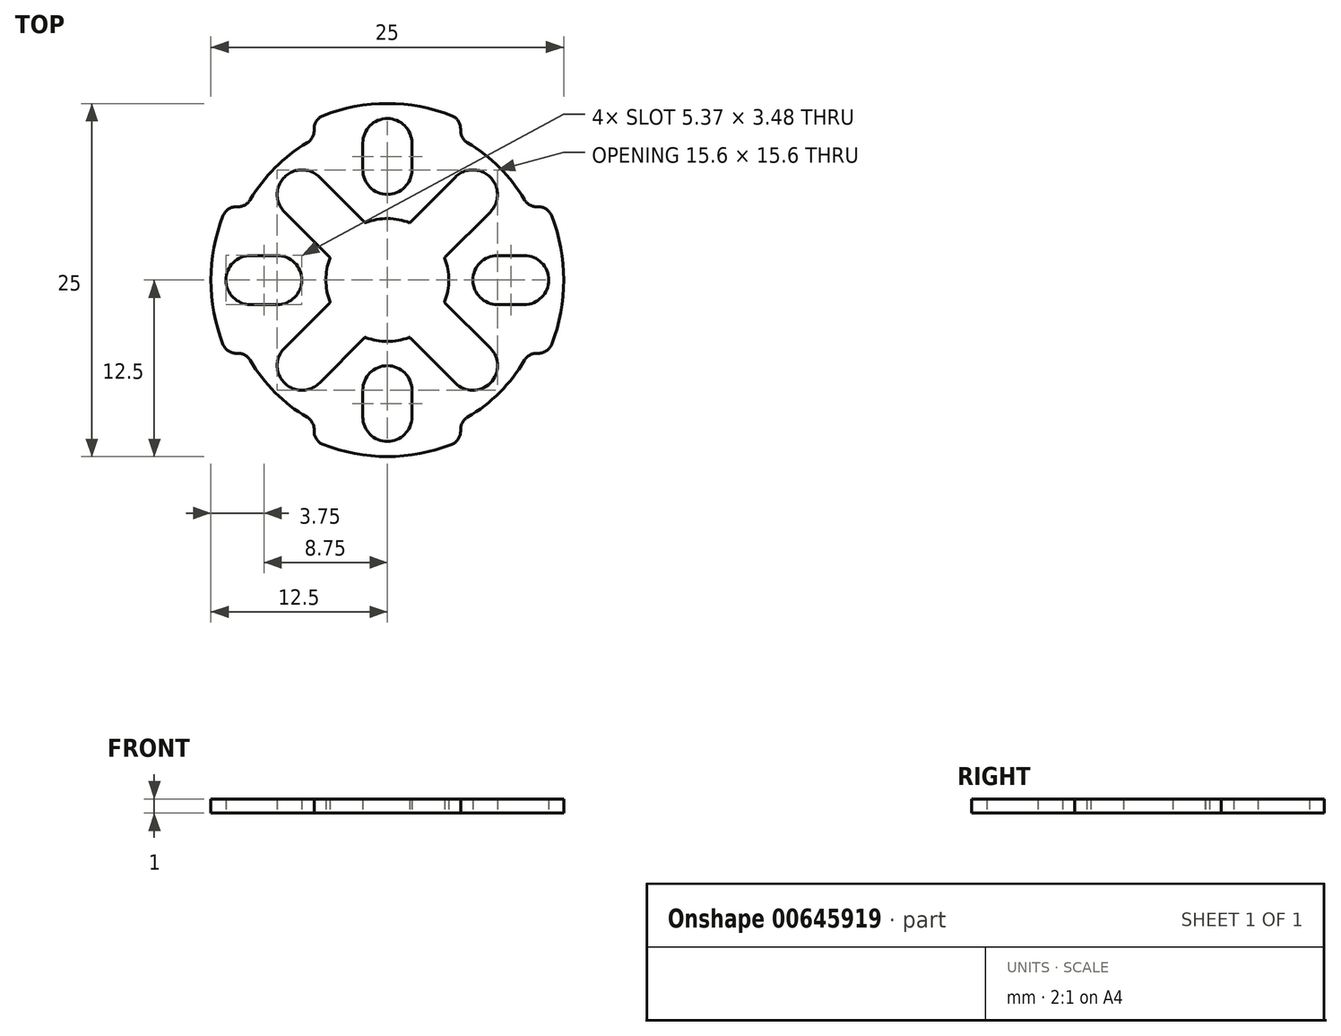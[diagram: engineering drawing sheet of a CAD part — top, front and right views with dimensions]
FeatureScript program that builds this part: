
annotation { "Feature Type Name" : "Feature", "Feature Type Description" : "" }
export const myFeature = defineFeature(function(context is Context, id is Id, definition is map)
    precondition{}
    {
        {
            var Q0;
            Q0=qCreatedBy(makeId("Top.planeOp"),FACE);
            var sketch = newSketch(context, id + "F0", { "sketchPlane" : qUnion([Q0])});
            skPoint(sketch, "E0.MirrorCS.start.orphan", {"position": v(0, 0) * mm});
            skPoint(sketch, "E1.visualSharp", {"position": v(12.16, 4.72) * mm});
            skPoint(sketch, "E2.MirrorCS.start.orphan", {"position": v(-6.94, 4.47) * mm});
            skPoint(sketch, "E3.orphan", {"position": v(-4.46, 2.26) * mm});
            skPoint(sketch, "E4.center.orphan", {"position": v(-6.07, 6.07) * mm});
            skPoint(sketch, "E5.MirrorCS.end.orphan", {"position": v(4.47, -6.94) * mm});
            skPoint(sketch, "E5.MirrorCS.start.orphan", {"position": v(6.94, -4.47) * mm});
            skPoint(sketch, "E6.start.orphan", {"position": v(-4.47, 6.94) * mm});
            skLineSegment(sketch, "E7", {"start": v(-4.6, 2.13) * mm, "end": v(-7.29, 4.81) * mm});
            skLineSegment(sketch, "E8.MirrorCS", {"start": v(-2.13, 4.6) * mm, "end": v(-4.81, 7.29) * mm});
            skPoint(sketch, "E9.MirrorCS.start.orphan", {"position": v(-4.47, -6.94) * mm});
            skPoint(sketch, "E10.MirrorCS.start.orphan", {"position": v(-6.94, -4.47) * mm});
            skPoint(sketch, "E11.MirrorCS.start.orphan", {"position": v(4.55, -2.08) * mm});
            skPoint(sketch, "E12.MirrorC.end.orphan", {"position": v(4.97, -7.45) * mm});
            skPoint(sketch, "E12.MirrorC.start.orphan", {"position": v(7.45, -4.97) * mm});
            skPoint(sketch, "E13.orphan", {"position": v(-7.45, 4.97) * mm});
            skPoint(sketch, "E14.orphan", {"position": v(-4.97, 7.45) * mm});
            skPoint(sketch, "E15.MirrorCS.end.orphan", {"position": v(4.97, 7.45) * mm});
            skPoint(sketch, "E15.MirrorCS.start.orphan", {"position": v(2.08, 4.55) * mm});
            skPoint(sketch, "E16.MirrorCS.start.orphan", {"position": v(4.55, 2.08) * mm});
            skPoint(sketch, "E17.MirrorCS.end.orphan", {"position": v(-4.97, -7.45) * mm});
            skPoint(sketch, "E17.MirrorCS.start.orphan", {"position": v(-2.08, -4.55) * mm});
            skPoint(sketch, "E18.MirrorCS.start.orphan", {"position": v(-7.45, -4.97) * mm});
            skPoint(sketch, "E19.MirrorCS.start.orphan", {"position": v(-4.55, -2.08) * mm});
            skLineSegment(sketch, "E20.MirrorCS", {"start": v(2.13, 4.6) * mm, "end": v(4.85, 7.32) * mm});
            skArc(sketch, "E21.MirrorCS", {"start": v(4.82, -7.3) * mm, "mid": v(6.06, -7.82) * mm, "end": v(7.3, -7.3) * mm});
            skLineSegment(sketch, "E22.MirrorCS", {"start": v(4.6, -2.13) * mm, "end": v(7.32, -4.85) * mm});
            skLineSegment(sketch, "E23.MirrorCS", {"start": v(-2.13, -4.6) * mm, "end": v(-4.85, -7.32) * mm});
            skLineSegment(sketch, "E24.MirrorCS", {"start": v(-4.6, -2.13) * mm, "end": v(-7.32, -4.85) * mm});
            skLineSegment(sketch, "E25.MirrorCS", {"start": v(2.13, -4.6) * mm, "end": v(4.82, -7.3) * mm});
            skArc(sketch, "E26", {"start": v(4.55, 11.64) * mm, "mid": v(0, 12.5) * mm, "end": v(-4.55, 11.64) * mm});
            skPoint(sketch, "E27.MirrorCS.end.orphan", {"position": v(10.93, 4.72) * mm});
            skPoint(sketch, "E1.filletArc.end.orphan", {"position": v(11.3, 4.72) * mm});
            skArc(sketch, "E28.filletArc", {"start": v(5.19, 10.7) * mm, "mid": v(5.02, 11.27) * mm, "end": v(4.55, 11.64) * mm});
            skArc(sketch, "E29.filletArc", {"start": v(-4.55, 11.64) * mm, "mid": v(-5.02, 11.27) * mm, "end": v(-5.19, 10.7) * mm});
            skArc(sketch, "E30", {"start": v(-5.68, 9.72) * mm, "mid": v(-7.96, 7.96) * mm, "end": v(-9.72, 5.68) * mm});
            skLineSegment(sketch, "E31", {"start": v(-5.19, 10.7) * mm, "end": v(-5.19, 10.58) * mm});
            skLineSegment(sketch, "E32", {"start": v(5.19, 10.7) * mm, "end": v(5.19, 10.58) * mm});
            skPoint(sketch, "E33.visualSharp", {"position": v(-5.19, 9.99) * mm});
            skArc(sketch, "E33.filletArc", {"start": v(-5.68, 9.72) * mm, "mid": v(-5.32, 10.08) * mm, "end": v(-5.19, 10.58) * mm});
            skPoint(sketch, "E34.visualSharp", {"position": v(5.19, 9.99) * mm});
            skArc(sketch, "E34.filletArc", {"start": v(5.19, 10.58) * mm, "mid": v(5.32, 10.08) * mm, "end": v(5.68, 9.72) * mm});
            skArc(sketch, "E35.MirrorCS", {"start": v(-4.55, -11.64) * mm, "mid": v(-5.02, -11.27) * mm, "end": v(-5.19, -10.7) * mm});
            skLineSegment(sketch, "E36.MirrorCS", {"start": v(5.19, -10.7) * mm, "end": v(5.19, -10.58) * mm});
            skArc(sketch, "E37.MirrorCS", {"start": v(5.19, -10.7) * mm, "mid": v(5.02, -11.27) * mm, "end": v(4.55, -11.64) * mm});
            skLineSegment(sketch, "E38.MirrorCS", {"start": v(-5.19, -10.7) * mm, "end": v(-5.19, -10.58) * mm});
            skArc(sketch, "E39.MirrorCS", {"start": v(4.55, -11.64) * mm, "mid": v(0, -12.5) * mm, "end": v(-4.55, -11.64) * mm});
            skPoint(sketch, "E40.MirrorP", {"position": v(-5.19, -9.99) * mm});
            skPoint(sketch, "E41.MirrorP", {"position": v(5.19, -9.99) * mm});
            skArc(sketch, "E42.MirrorCS", {"start": v(-5.68, -9.72) * mm, "mid": v(-5.32, -10.08) * mm, "end": v(-5.19, -10.58) * mm});
            skArc(sketch, "E43.MirrorCS", {"start": v(5.19, -10.58) * mm, "mid": v(5.32, -10.08) * mm, "end": v(5.68, -9.72) * mm});
            skArc(sketch, "E44.MirrorCS", {"start": v(-11.64, 4.55) * mm, "mid": v(-12.5, 0) * mm, "end": v(-11.64, -4.55) * mm});
            skArc(sketch, "E45.MirrorCS", {"start": v(-10.7, 5.19) * mm, "mid": v(-11.27, 5.02) * mm, "end": v(-11.64, 4.55) * mm});
            skLineSegment(sketch, "E46.MirrorCS", {"start": v(-10.7, 5.19) * mm, "end": v(-10.58, 5.19) * mm});
            skArc(sketch, "E47.MirrorCS", {"start": v(-10.58, 5.19) * mm, "mid": v(-10.08, 5.32) * mm, "end": v(-9.72, 5.68) * mm});
            skArc(sketch, "E48.MirrorCS", {"start": v(-9.72, -5.68) * mm, "mid": v(-10.08, -5.32) * mm, "end": v(-10.58, -5.19) * mm});
            skLineSegment(sketch, "E49.MirrorCS", {"start": v(-10.7, -5.19) * mm, "end": v(-10.58, -5.19) * mm});
            skArc(sketch, "E50.MirrorCS", {"start": v(-11.64, -4.55) * mm, "mid": v(-11.27, -5.02) * mm, "end": v(-10.7, -5.19) * mm});
            skArc(sketch, "E51.MirrorCS", {"start": v(11.64, 4.55) * mm, "mid": v(12.5, 0) * mm, "end": v(11.64, -4.55) * mm});
            skArc(sketch, "E52.MirrorCS", {"start": v(11.64, -4.55) * mm, "mid": v(11.27, -5.02) * mm, "end": v(10.7, -5.19) * mm});
            skArc(sketch, "E53.MirrorCS", {"start": v(9.72, -5.68) * mm, "mid": v(10.08, -5.32) * mm, "end": v(10.58, -5.19) * mm});
            skLineSegment(sketch, "E54.MirrorCS", {"start": v(10.7, -5.19) * mm, "end": v(10.58, -5.19) * mm});
            skArc(sketch, "E55.MirrorCS", {"start": v(10.7, 5.19) * mm, "mid": v(11.27, 5.02) * mm, "end": v(11.64, 4.55) * mm});
            skArc(sketch, "E56.MirrorCS", {"start": v(10.58, 5.19) * mm, "mid": v(10.08, 5.32) * mm, "end": v(9.72, 5.68) * mm});
            skLineSegment(sketch, "E57.MirrorCS", {"start": v(10.7, 5.19) * mm, "end": v(10.58, 5.19) * mm});
            skArc(sketch, "E58.trimOffspring", {"start": v(-9.72, -5.68) * mm, "mid": v(-7.96, -7.96) * mm, "end": v(-5.68, -9.72) * mm});
            skArc(sketch, "E59.trimOffspring", {"start": v(9.72, 5.68) * mm, "mid": v(7.96, 7.96) * mm, "end": v(5.68, 9.72) * mm});
            skArc(sketch, "E60.trimOffspring", {"start": v(5.68, -9.72) * mm, "mid": v(7.96, -7.96) * mm, "end": v(9.72, -5.68) * mm});
            skCircle(sketch, "E61", {"center": v(0, 0) * mm, "radius": 12.5 * mm, "construction": true});
            skLineSegment(sketch, "E62", {"start": v(0, 0) * mm, "end": v(9.97, -9.97) * mm, "construction": true});
            skLineSegment(sketch, "E63.MirrorCS", {"start": v(4.6, 2.13) * mm, "end": v(7.32, 4.85) * mm});
            skPoint(sketch, "E64.visualSharp", {"position": v(2.08, -4.55) * mm});
            skPoint(sketch, "E65.visualSharp", {"position": v(-2.08, 4.55) * mm});
            skPoint(sketch, "E66.MirrorCS.end.orphan", {"position": v(-1.74, -7.8) * mm});
            skPoint(sketch, "E67.MirrorCS.start.orphan", {"position": v(-1.74, -9.7) * mm});
            skLineSegment(sketch, "E68", {"start": v(-1.74, -7.8) * mm, "end": v(-1.74, -9.7) * mm});
            skLineSegment(sketch, "E69.MirrorCS", {"start": v(1.74, -7.8) * mm, "end": v(1.74, -9.7) * mm});
            skArc(sketch, "E70", {"start": v(1.74, -9.7) * mm, "mid": v(0, -11.44) * mm, "end": v(-1.74, -9.7) * mm});
            skArc(sketch, "E71", {"start": v(1.74, -7.8) * mm, "mid": v(0, -6.06) * mm, "end": v(-1.74, -7.8) * mm});
            skPoint(sketch, "E72.MirrorP", {"position": v(-1.74, 7.8) * mm});
            skPoint(sketch, "E73.MirrorP", {"position": v(-1.74, 9.7) * mm});
            skArc(sketch, "E74.MirrorCS", {"start": v(1.74, 7.8) * mm, "mid": v(0, 6.06) * mm, "end": v(-1.74, 7.8) * mm});
            skLineSegment(sketch, "E75.MirrorCS", {"start": v(-1.74, 7.8) * mm, "end": v(-1.74, 9.7) * mm});
            skLineSegment(sketch, "E76.MirrorCS", {"start": v(1.74, 7.8) * mm, "end": v(1.74, 9.7) * mm});
            skArc(sketch, "E77.MirrorCS", {"start": v(1.74, 9.7) * mm, "mid": v(0, 11.44) * mm, "end": v(-1.74, 9.7) * mm});
            skPoint(sketch, "E78.MirrorP", {"position": v(7.8, 1.74) * mm});
            skPoint(sketch, "E79.MirrorP", {"position": v(9.7, 1.74) * mm});
            skArc(sketch, "E80.MirrorCS", {"start": v(7.8, -1.74) * mm, "mid": v(6.06, 0) * mm, "end": v(7.8, 1.74) * mm});
            skLineSegment(sketch, "E81.MirrorCS", {"start": v(7.8, -1.74) * mm, "end": v(9.7, -1.74) * mm});
            skArc(sketch, "E82.MirrorCS", {"start": v(9.7, -1.74) * mm, "mid": v(11.44, 0) * mm, "end": v(9.7, 1.74) * mm});
            skLineSegment(sketch, "E83.MirrorCS", {"start": v(7.8, 1.74) * mm, "end": v(9.7, 1.74) * mm});
            skArc(sketch, "E84.MirrorCS", {"start": v(-9.7, -1.74) * mm, "mid": v(-11.44, 0) * mm, "end": v(-9.7, 1.74) * mm});
            skArc(sketch, "E85.MirrorCS", {"start": v(-7.8, -1.74) * mm, "mid": v(-6.06, 0) * mm, "end": v(-7.8, 1.74) * mm});
            skLineSegment(sketch, "E86.MirrorCS", {"start": v(-7.8, -1.74) * mm, "end": v(-9.7, -1.74) * mm});
            skLineSegment(sketch, "E87", {"start": v(-9.7, 1.74) * mm, "end": v(-7.8, 1.74) * mm});
            skPoint(sketch, "E88.visualSharp", {"position": v(-4.55, 2.08) * mm});
            skArc(sketch, "E89", {"start": v(-4.81, 7.29) * mm, "mid": v(-7.29, 7.29) * mm, "end": v(-7.29, 4.81) * mm});
            skPoint(sketch, "E90.MirrorCS.end.orphan", {"position": v(7.32, 4.85) * mm});
            skPoint(sketch, "E90.MirrorCS.start.orphan", {"position": v(4.85, 7.32) * mm});
            skPoint(sketch, "E91.orphan", {"position": v(7.32, -4.85) * mm});
            skPoint(sketch, "E92.MirrorCS.end.orphan", {"position": v(-7.32, -4.85) * mm});
            skPoint(sketch, "E92.MirrorCS.start.orphan", {"position": v(-4.85, -7.32) * mm});
            skArc(sketch, "E93.MirrorCS", {"start": v(4.81, 7.29) * mm, "mid": v(7.29, 7.29) * mm, "end": v(7.29, 4.81) * mm});
            skArc(sketch, "E94.MirrorCS", {"start": v(-4.81, -7.29) * mm, "mid": v(-7.29, -7.29) * mm, "end": v(-7.29, -4.81) * mm});
            skArc(sketch, "E95.MirrorCS", {"start": v(4.81, -7.29) * mm, "mid": v(7.29, -7.29) * mm, "end": v(7.29, -4.81) * mm});
            skLineSegment(sketch, "E96", {"start": v(-2.13, -4.6) * mm, "end": v(-1.63, -4.1) * mm});
            skLineSegment(sketch, "E97.MirrorCS", {"start": v(2.13, -4.6) * mm, "end": v(1.63, -4.1) * mm});
            skLineSegment(sketch, "E98", {"start": v(-4.6, -2.13) * mm, "end": v(-4.1, -1.63) * mm});
            skLineSegment(sketch, "E99", {"start": v(-4.6, 2.13) * mm, "end": v(-4.1, 1.63) * mm});
            skLineSegment(sketch, "E100.MirrorCS", {"start": v(4.6, 2.13) * mm, "end": v(4.1, 1.63) * mm});
            skLineSegment(sketch, "E101.MirrorCS", {"start": v(4.6, -2.13) * mm, "end": v(4.1, -1.63) * mm});
            skLineSegment(sketch, "E102.MirrorCS", {"start": v(-2.13, 4.6) * mm, "end": v(-1.63, 4.1) * mm});
            skLineSegment(sketch, "E103.MirrorCS", {"start": v(2.13, 4.6) * mm, "end": v(1.58, 4.05) * mm});
            skPoint(sketch, "E104.visualSharp", {"position": v(-1.5, 3.97) * mm});
            skPoint(sketch, "E105.visualSharp", {"position": v(1.5, 3.97) * mm});
            skPoint(sketch, "E106.visualSharp", {"position": v(3.97, 1.5) * mm});
            skPoint(sketch, "E107.visualSharp", {"position": v(3.97, -1.5) * mm});
            skPoint(sketch, "E108.visualSharp", {"position": v(1.5, -3.97) * mm});
            skPoint(sketch, "E109.visualSharp", {"position": v(-1.5, -3.97) * mm});
            skPoint(sketch, "E110.visualSharp", {"position": v(-3.97, -1.5) * mm});
            skPoint(sketch, "E111.visualSharp", {"position": v(-3.97, 1.5) * mm});
            skArc(sketch, "E112", {"start": v(1.58, 4.05) * mm, "mid": v(0.03, 4.35) * mm, "end": v(-1.52, 4.08) * mm});
            skArc(sketch, "E113.trimOffspring", {"start": v(4.08, -1.52) * mm, "mid": v(4.35, 0) * mm, "end": v(4.08, 1.52) * mm});
            skArc(sketch, "E114.trimOffspring", {"start": v(-1.52, -4.08) * mm, "mid": v(0, -4.35) * mm, "end": v(1.52, -4.08) * mm});
            skArc(sketch, "E115.trimOffspring", {"start": v(-4.08, 1.52) * mm, "mid": v(-4.35, 0) * mm, "end": v(-4.08, -1.52) * mm});
            skPoint(sketch, "E116.visualSharp", {"position": v(-1.58, 4.05) * mm});
            skArc(sketch, "E116.filletArc", {"start": v(-1.63, 4.1) * mm, "mid": v(-1.58, 4.07) * mm, "end": v(-1.52, 4.08) * mm});
            skPoint(sketch, "E117.visualSharp", {"position": v(-4.05, 1.58) * mm});
            skArc(sketch, "E117.filletArc", {"start": v(-4.08, 1.52) * mm, "mid": v(-4.07, 1.58) * mm, "end": v(-4.1, 1.63) * mm});
            skPoint(sketch, "E118.visualSharp", {"position": v(-4.05, -1.58) * mm});
            skArc(sketch, "E118.filletArc", {"start": v(-4.1, -1.63) * mm, "mid": v(-4.07, -1.58) * mm, "end": v(-4.08, -1.52) * mm});
            skPoint(sketch, "E119.visualSharp", {"position": v(4.05, 1.58) * mm});
            skArc(sketch, "E119.filletArc", {"start": v(4.1, 1.63) * mm, "mid": v(4.07, 1.58) * mm, "end": v(4.08, 1.52) * mm});
            skPoint(sketch, "E120.visualSharp", {"position": v(4.05, -1.58) * mm});
            skArc(sketch, "E120.filletArc", {"start": v(4.08, -1.52) * mm, "mid": v(4.07, -1.58) * mm, "end": v(4.1, -1.63) * mm});
            skPoint(sketch, "E121.visualSharp", {"position": v(1.58, -4.05) * mm});
            skArc(sketch, "E121.filletArc", {"start": v(1.63, -4.1) * mm, "mid": v(1.58, -4.07) * mm, "end": v(1.52, -4.08) * mm});
            skPoint(sketch, "E122.visualSharp", {"position": v(-1.58, -4.05) * mm});
            skArc(sketch, "E122.filletArc", {"start": v(-1.52, -4.08) * mm, "mid": v(-1.58, -4.07) * mm, "end": v(-1.63, -4.1) * mm});
            skSolve(sketch);
        }
        {
            var Q0;
            Q0 = qSketchRegion(id + "F0", true);
            extrude(context, id + "F1", {"entities" : qUnion([Q0]), "depth" : 1 * mm, "offsetDistance" : 25 * mm});
        }
    });
